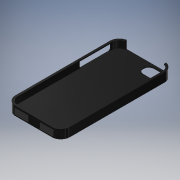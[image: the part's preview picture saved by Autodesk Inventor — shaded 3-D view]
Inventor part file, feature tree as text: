
AUTODESK INVENTOR PART (.ipt)
format: ipt  version: 2019 (Build 230136000, 136)  size: 370,688 bytes
history: native  units: mm
features: sketch x15, extrude x14, other x1, sweep x1, fillet x1
ambient origin geometry x8: Origin, YZ Plane, XZ Plane, XY Plane, X Axis, Y Axis, Z Axis, Center Point
bodies: Body1 (feature_tree)
feature tree (32):
  other  "솔리드1"
  extrude  "돌출1"  Depth=124.3mm
  sketch  "Sketch2"  dims[d0=59.0mm d1=124.3mm]
  sweep  "스윕1"
  extrude  "돌출2"  Depth=8.9mm
  extrude  "돌출3"  TaperAngle=0.0deg  [1 undecoded]
  extrude  "돌출6"  Depth=1.0mm
  extrude  "Extrusion8"  TaperAngle=0.0deg  [1 undecoded]
  fillet  "Fillet8"  Radius=44.0mm
  extrude  "Extrusion9"  Depth=22.0mm
  extrude  "Extrusion10"  Depth=6.0mm
  extrude  "Extrusion11"  Depth=2.0mm
  extrude  "Extrusion12"  Depth=1.0mm TaperAngle=0.0deg
  extrude  "Extrusion13"  Depth=1.0mm
  extrude  "Extrusion14"  TaperAngle=0.0deg  [1 undecoded]
  extrude  "Extrusion15"  Depth=9.9mm
  extrude  "Extrusion16"  TaperAngle=90.0deg  [1 undecoded]
  extrude  "Extrusion17"  Depth=2.3mm
  sketch  "스케치1"
  sketch  "스케치5"
  sketch  "스케치6"
  sketch  "스케치9"
  sketch  "Sketch12"  dims[d2=9.3mm d3=1.0mm d4=0.0mm]
  sketch  "Sketch13"  dims[d5=8.9mm d6=1.3mm]
  sketch  "Sketch14"  dims[d7=1.0mm d9=0.0mm]
  sketch  "Sketch15"  dims[d12=44.0mm d13=1.0mm]
  sketch  "Sketch16"  dims[d14=22.0mm d15=0.0mm d16=0.0mm d17=44.0mm]
  sketch  "Sketch17"  dims[d18=22.0mm d19=62.15mm]
  sketch  "Sketch18"  dims[d20=1.0mm d21=0.0mm d36=6.0mm]
  sketch  "Sketch19"  dims[d37=8.0mm d38=2.0mm]
  sketch  "Sketch20"  dims[d39=11.5mm d40=1.0mm d41=0.0mm]
  sketch  "Sketch21"  dims[d44=0.0mm d45=1.0mm d46=0.0mm d47=9.9mm d48=90.0deg d50=2.3mm d51=35.0mm d52=90.0deg d53=8.9mm d54=90.0deg d55=35.0mm d56=90.0deg d57=8.9mm d58=90.0deg d59=1.5mm d60=180.0deg d61=35.0mm d62=90.0deg d63=7.4mm d64=35.0mm d65=10.0mm d66=0.0mm d67=2.0mm d68=44.0mm d69=1.0mm d70=0.8415mm d71=0.0mm d72=44.0mm d73=1.0mm d74=0.8415mm d75=0.0mm d76=22.0mm d77=180.0deg d78=6.0mm d79=1.0mm d80=6.0mm d81=1.0mm d82=8.9mm d83=0.0mm d84=1.0mm d85=2.347mm d86=44.0mm d87=0.0mm d88=1.0mm d89=1.017mm d90=21.0mm d91=90.0deg d92=0.5mm d93=85.0mm d94=0.5mm d95=85.0mm d96=2.1mm d97=0.0mm d98=1.0mm d99=85.0mm d100=1.1mm d101=2.1mm d102=0.0mm d103=0.0mm d104=24.7mm d105=180.0deg d106=1.0mm d107=85.0mm d108=24.7mm d109=0.0mm d110=1.0mm d111=85.0mm d112=2.1mm d113=0.0mm d114=1.0mm d115=85.0mm d116=1.0mm d117=0.0mm d118=1.0mm d119=85.0mm d120=1.0mm d121=0.0mm]
note: 4 required parameter values undecoded (feature->parameter linkage not recoverable at this tier; creation-order binding heuristic only, values carry confidence <= 0.55)
